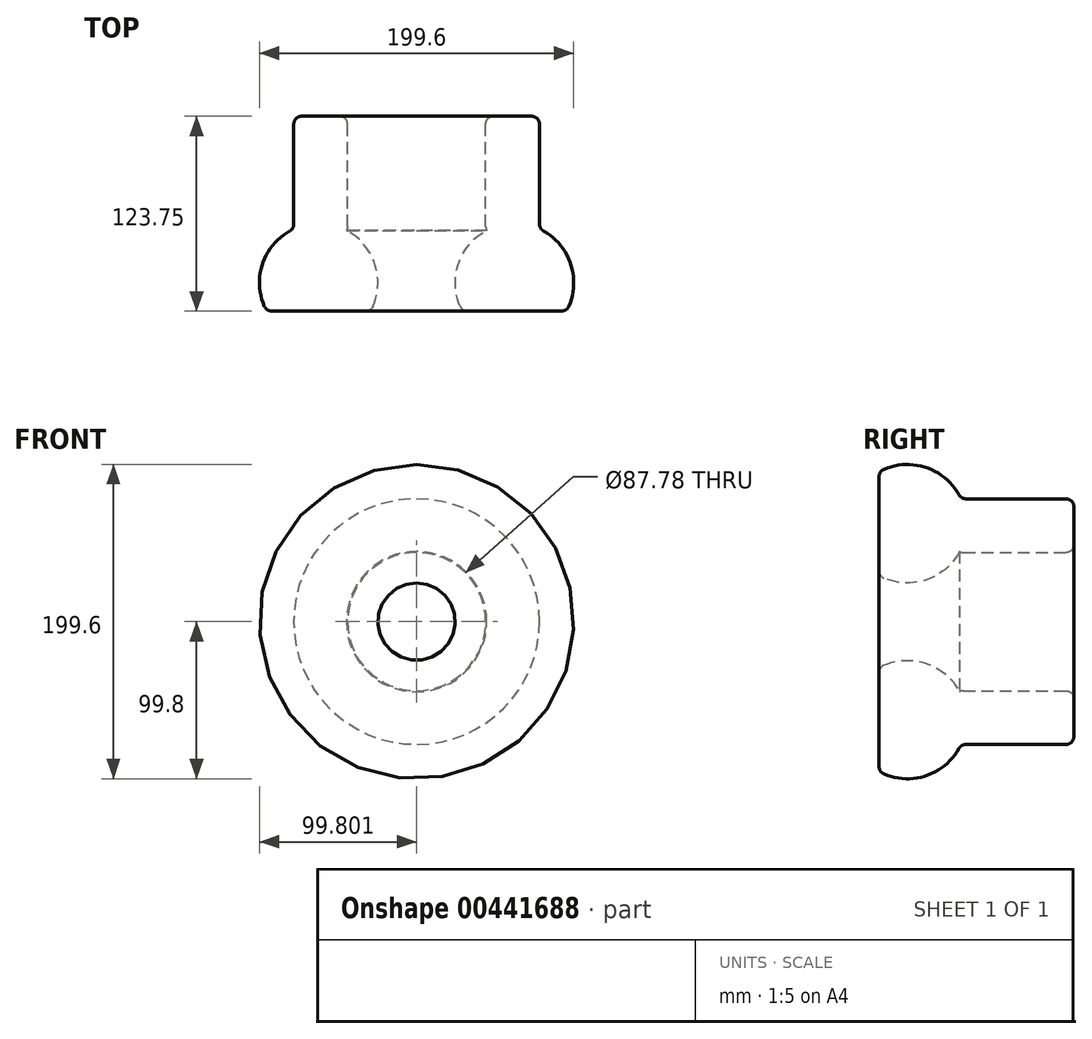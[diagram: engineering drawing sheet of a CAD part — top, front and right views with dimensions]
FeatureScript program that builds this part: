
annotation { "Feature Type Name" : "Feature", "Feature Type Description" : "" }
export const myFeature = defineFeature(function(context is Context, id is Id, definition is map)
    precondition{}
    {
        {
            var Q0;
            Q0=qCreatedBy(makeId("Top.planeOp"),FACE);
            var sketch = newSketch(context, id + "F0", { "sketchPlane" : qUnion([Q0])});
            skLineSegment(sketch, "E0.bottom", {"start": v(-18.29, 59.59) * mm, "end": v(15.85, 59.59) * mm});
            skLineSegment(sketch, "E0.top", {"start": v(-18.29, -12.95) * mm, "end": v(15.85, -12.95) * mm});
            skLineSegment(sketch, "E0.left", {"start": v(-18.29, 59.59) * mm, "end": v(-18.29, -12.95) * mm});
            skLineSegment(sketch, "E0.right", {"start": v(15.85, 59.59) * mm, "end": v(15.85, -12.95) * mm});
            skArc(sketch, "E1", {"start": v(-17.65, -12.95) * mm, "mid": v(-36.03, -35.35) * mm, "end": v(-33.05, -64.16) * mm});
            skLineSegment(sketch, "E2", {"start": v(-33.05, -64.16) * mm, "end": v(33.05, -64.16) * mm});
            skArc(sketch, "E3.trimOffspring", {"start": v(33.05, -64.16) * mm, "mid": v(35.73, -34.39) * mm, "end": v(15.85, -12.06) * mm});
            skLineSegment(sketch, "E4", {"start": v(-62.18, 71.17) * mm, "end": v(-62.18, -72.4) * mm});
            skSolve(sketch);
        }
        {
            var Q0;
            {var subQ5=sQuery(id+"F0.wireOp",EDGE,"E0.bottom");Q0=makeQuery(id+"F0.imprint","IMPRINT",FACE,{"disambiguationData":[TD([[makeQuery(id+"F0.imprint","IMPRINT",EDGE,{"derivedFrom":subQ5}),-1.0]])]});}
            var Q1;
            {var subQ0=sQuery(id+"F0.wireOp",EDGE,"E1");Q1=makeQuery(id+"F0.imprint","IMPRINT",FACE,{"disambiguationData":[TD([[makeQuery(id+"F0.imprint","IMPRINT",EDGE,{"derivedFrom":subQ0}),1.0]])]});}
            var Q2;
            Q2=sQuery(id+"F0.wireOp",EDGE,"E4");
            revolve(context, id + "F1", {"entities" : qUnion([Q0, Q1]), "axis" : qUnion([Q2]), "revolveType" : RevolveType.FULL});
        }
        {
            var Q0;
            Q0=makeQuery(id+"F1.opRevolve","SWEPT_EDGE",EDGE,{"disambiguationData":[OSD([sQuery(id+"F0.wireOp",EDGE,"E2"),sQuery(id+"F0.wireOp",EDGE,"E3.trimOffspring")])]});
            var Q1;
            Q1=makeQuery(id+"F1.opRevolve","SWEPT_EDGE",EDGE,{"disambiguationData":[OSD([sQuery(id+"F0.wireOp",EDGE,"E0.bottom"),sQuery(id+"F0.wireOp",EDGE,"E0.right")])]});
            fillet(context, id + "F2", {"entities" : qUnion([Q0, Q1]), "radius" : 5.08 * mm, "tangentPropagation" : true, "allowEdgeOverflow" : false});
        }
        {
            var Q0;
            Q0=makeQuery(id+"F1.opRevolve","SWEPT_EDGE",EDGE,{"disambiguationData":[OSD([sQuery(id+"F0.wireOp",EDGE,"E0.right"),sQuery(id+"F0.wireOp",EDGE,"E3.trimOffspring")])]});
            fillet(context, id + "F3", {"entities" : qUnion([Q0]), "radius" : 5.08 * mm, "tangentPropagation" : true, "allowEdgeOverflow" : false});
        }
        {
            var Q0;
            Q0=makeQuery(id+"F1.opRevolve","SWEPT_EDGE",EDGE,{"disambiguationData":[OSD([sQuery(id+"F0.wireOp",EDGE,"E0.bottom"),sQuery(id+"F0.wireOp",EDGE,"E0.left")])]});
            var Q1;
            Q1=makeQuery(id+"F1.opRevolve","SWEPT_EDGE",EDGE,{"disambiguationData":[OSD([sQuery(id+"F0.wireOp",EDGE,"E0.top"),sQuery(id+"F0.wireOp",EDGE,"E0.left")])]});
            var Q2;
            Q2=makeQuery(id+"F1.opRevolve","SWEPT_EDGE",EDGE,{"disambiguationData":[OSD([sQuery(id+"F0.wireOp",EDGE,"E1"),sQuery(id+"F0.wireOp",EDGE,"E2")])]});
            fillet(context, id + "F4", {"entities" : qUnion([Q0, Q1, Q2]), "radius" : 5.08 * mm, "tangentPropagation" : true, "allowEdgeOverflow" : false});
        }
    });
